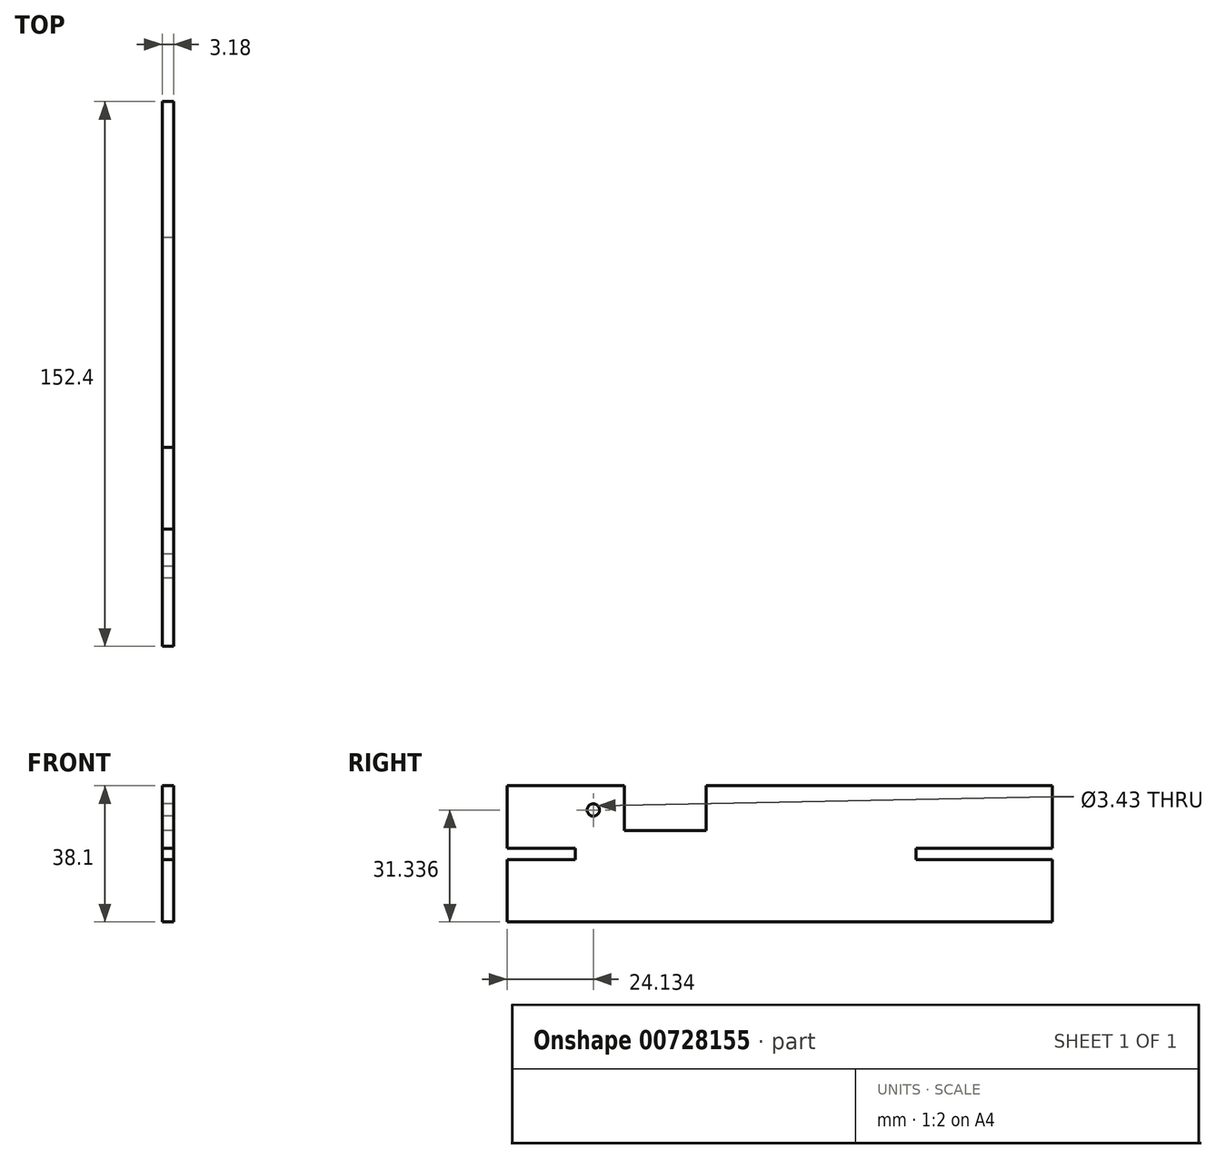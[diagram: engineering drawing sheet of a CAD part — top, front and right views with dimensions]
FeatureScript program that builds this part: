
annotation { "Feature Type Name" : "Feature", "Feature Type Description" : "" }
export const myFeature = defineFeature(function(context is Context, id is Id, definition is map)
    precondition{}
    {
        {
            var Q0;
            Q0=qCreatedBy(makeId("Right.planeOp"),FACE);
            var sketch = newSketch(context, id + "F0", { "sketchPlane" : qUnion([Q0])});
            skLineSegment(sketch, "E0", {"start": v(-74.58, 11.42) * mm, "end": v(77.82, 11.42) * mm});
            skLineSegment(sketch, "E1", {"start": v(77.82, 11.42) * mm, "end": v(77.82, -26.68) * mm});
            skLineSegment(sketch, "E2", {"start": v(77.82, -26.68) * mm, "end": v(-74.58, -26.68) * mm});
            skLineSegment(sketch, "E3", {"start": v(-74.58, -26.68) * mm, "end": v(-74.58, 11.42) * mm});
            skLineSegment(sketch, "E4", {"start": v(-74.58, -7.63) * mm, "end": v(77.82, -7.63) * mm});
            skLineSegment(sketch, "E5", {"start": v(-41.8, 11.42) * mm, "end": v(-41.8, -1.08) * mm});
            skLineSegment(sketch, "E6", {"start": v(-41.8, -1.08) * mm, "end": v(-18.94, -1.08) * mm});
            skLineSegment(sketch, "E7", {"start": v(-18.94, -1.08) * mm, "end": v(-18.94, 11.42) * mm});
            skLineSegment(sketch, "E8", {"start": v(-74.58, -6.04) * mm, "end": v(-55.53, -6.04) * mm});
            skLineSegment(sketch, "E9.MirrorCS", {"start": v(-74.58, -9.22) * mm, "end": v(-55.53, -9.22) * mm});
            skLineSegment(sketch, "E10", {"start": v(-55.53, -6.04) * mm, "end": v(-55.53, -9.22) * mm});
            skLineSegment(sketch, "E11.MirrorCS", {"start": v(65.12, -7.66) * mm, "end": v(39.72, -7.66) * mm});
            skCircle(sketch, "E12.MirrorC", {"center": v(-50.45, 4.66) * mm, "radius": 1.71 * mm});
            skPoint(sketch, "E13", {"position": v(-30.38, -1.08) * mm});
            skLineSegment(sketch, "E14", {"start": v(1.62, -26.68) * mm, "end": v(1.62, -23.18) * mm});
            skLineSegment(sketch, "E15.MirrorCS", {"start": v(77.82, -9.22) * mm, "end": v(58.77, -9.22) * mm});
            skLineSegment(sketch, "E16.MirrorCS", {"start": v(77.82, -6.04) * mm, "end": v(58.77, -6.04) * mm});
            skLineSegment(sketch, "E17", {"start": v(58.77, -6.04) * mm, "end": v(39.72, -6.04) * mm});
            skLineSegment(sketch, "E18.MirrorCS", {"start": v(58.77, -9.22) * mm, "end": v(39.72, -9.22) * mm});
            skLineSegment(sketch, "E19", {"start": v(39.72, -7.66) * mm, "end": v(39.72, -9.22) * mm});
            skLineSegment(sketch, "E20", {"start": v(39.72, -6.04) * mm, "end": v(39.72, -7.66) * mm});
            skSolve(sketch);
        }
        {
            var Q0;
            {var subQ14=sQuery(id+"F0.wireOp",EDGE,"E5");Q0=makeQuery(id+"F0.imprint","IMPRINT",FACE,{"disambiguationData":[TD([[makeQuery(id+"F0.imprint","IMPRINT",EDGE,{"derivedFrom":subQ14}),-1.0]])]});}
            var Q1;
            {var subQ5=sQuery(id+"F0.wireOp",EDGE,"E2");Q1=makeQuery(id+"F0.imprint","IMPRINT",FACE,{"disambiguationData":[TD([[makeQuery(id+"F0.imprint","IMPRINT",EDGE,{"derivedFrom":subQ5}),-1.0]])]});}
            extrude(context, id + "F1", {"entities" : qUnion([Q0, Q1]), "depth" : 3.17 * mm, "offsetDistance" : 25.4 * mm});
        }
    });
